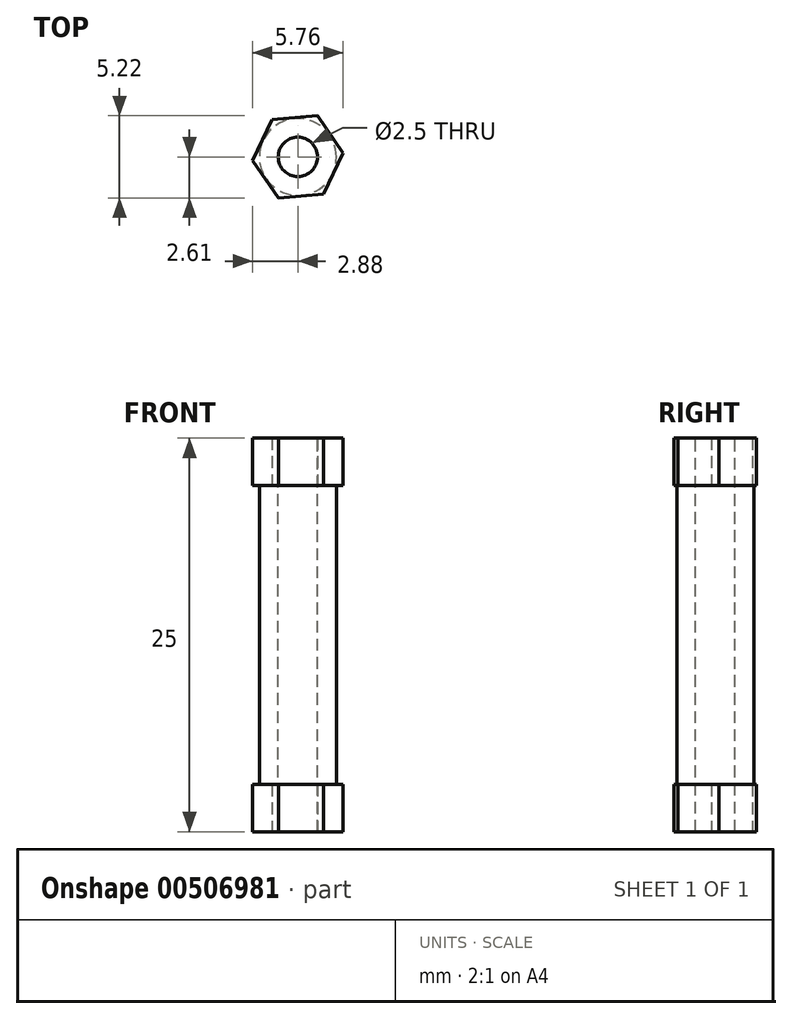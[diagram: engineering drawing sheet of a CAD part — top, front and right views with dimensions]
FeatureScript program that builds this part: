
annotation { "Feature Type Name" : "Feature", "Feature Type Description" : "" }
export const myFeature = defineFeature(function(context is Context, id is Id, definition is map)
    precondition{}
    {
        {
            var Q0;
            Q0=qCreatedBy(makeId("Top.planeOp"),FACE);
            var sketch = newSketch(context, id + "F0", { "sketchPlane" : qUnion([Q0])});
            skCircle(sketch, "E0", {"center": v(0, 0) * mm, "radius": 2.5 * mm, "construction": true});
            skLineSegment(sketch, "E1.0", {"start": v(2.88, 0.24) * mm, "end": v(1.64, -2.37) * mm});
            skLineSegment(sketch, "E1.1", {"start": v(1.64, -2.37) * mm, "end": v(-1.23, -2.6) * mm});
            skLineSegment(sketch, "E1.2", {"start": v(-1.23, -2.6) * mm, "end": v(-2.88, -0.24) * mm});
            skLineSegment(sketch, "E1.3", {"start": v(-2.88, -0.24) * mm, "end": v(-1.64, 2.37) * mm});
            skLineSegment(sketch, "E1.4", {"start": v(-1.64, 2.37) * mm, "end": v(1.23, 2.6) * mm});
            skLineSegment(sketch, "E1.5", {"start": v(1.23, 2.6) * mm, "end": v(2.88, 0.24) * mm});
            skPoint(sketch, "E1.0.midPoint", {"position": v(2.26, -1.07) * mm});
            skSolve(sketch);
        }
        {
            var Q0;
            Q0=makeQuery(id+"F0.imprint","IMPRINT",FACE,{"disambiguationData":[TD([[makeQuery(id+"F0.imprint","IMPRINT",EDGE,{"derivedFrom":sQuery(id+"F0.wireOp",EDGE,"E0")}),1.0]])]});
            var Q1;
            Q1=makeQuery(id+"F0.imprint","IMPRINT",FACE,{"disambiguationData":[TD([[makeQuery(id+"F0.imprint","IMPRINT",EDGE,{"derivedFrom":sQuery(id+"F0.wireOp",EDGE,"E1.0")}),-1.0]])]});
            var Q2;
            Q2=sQuery(id+"F0.wireOp",EDGE,"E0");
            extrude(context, id + "F1", {"entities" : qUnion([Q0, Q1]), "surfaceEntities" : qUnion([Q2]), "depth" : 25 * mm, "offsetDistance" : 25 * mm});
        }
        {
            var Q0;
            Q0=makeQuery(id+"F1.opExtrude","CAP_FACE",FACE,{"disambiguationData":[OSD([sQuery(id+"F0.wireOp",EDGE,"E1.0"),sQuery(id+"F0.wireOp",EDGE,"E1.1"),sQuery(id+"F0.wireOp",EDGE,"E1.2"),sQuery(id+"F0.wireOp",EDGE,"E1.3"),sQuery(id+"F0.wireOp",EDGE,"E1.4"),sQuery(id+"F0.wireOp",EDGE,"E1.5")])],"isStart":false});
            var sketch = newSketch(context, id + "F2", { "sketchPlane" : qUnion([Q0])});
            skPoint(sketch, "E2.0", {"position": v(0, 0) * mm});
            skSolve(sketch);
        }
        {
            var Q0;
            Q0=sQuery(id+"F2.wireOp",VERTEX,"E2.0");
            var Q1;
            Q1=makeQuery(id+"F1.opExtrude","SWEPT_BODY",BODY,{"disambiguationData":[OSD([sQuery(id+"F0.wireOp",EDGE,"E0")])]});
            var Q2;
            Q2=makeQuery(id+"F1.opExtrude","SWEPT_BODY",BODY,{"disambiguationData":[OSD([sQuery(id+"F0.wireOp",EDGE,"E1.0"),sQuery(id+"F0.wireOp",EDGE,"E1.1"),sQuery(id+"F0.wireOp",EDGE,"E1.2"),sQuery(id+"F0.wireOp",EDGE,"E1.3"),sQuery(id+"F0.wireOp",EDGE,"E1.4"),sQuery(id+"F0.wireOp",EDGE,"E1.5")])]});
            hole(context, id + "F3", {"style" : HoleStyle.SIMPLE, "endStyle" : HoleEndStyle.THROUGH, "standardTappedOrClearance" : lookupTablePath({ "standard" : "ISO", "engagement" : "75%", "pitch" : "0.5 mm", "size" : "M3", "type" : "Tapped" }), "standardBlindInLast" : lookupTablePath({ "standard" : "ISO", "engagement" : "75%", "pitch" : "0.5 mm", "size" : "M3", "type" : "Tapped" }), "holeDiameter" : 2.5 * mm, "showTappedDepth" : true, "isTappedThrough" : true, "tappedDepth" : 12 * mm, "tapClearance" : 3, "startFromSketch" : true, "locations" : qUnion([Q0]), "scope" : qUnion([Q1, Q2]), "majorDiameter" : 3 * mm});
        }
        {
            var Q0;
            Q0=qCreatedBy(makeId("Top.planeOp"),FACE);
            cPlane(context, id + "F4", {"entities" : qUnion([Q0]), "cplaneType" : CPlaneType.OFFSET, "offset" : 3 * mm, "width" : 150 * mm, "height" : 150 * mm});
        }
        {
            var Q0;
            Q0=qCreatedBy(id+"F4.planeOp",FACE);
            var sketch = newSketch(context, id + "F5", { "sketchPlane" : qUnion([Q0])});
            skPoint(sketch, "E3.0", {"position": v(0, 0) * mm});
            skCircle(sketch, "E4", {"center": v(0, 0) * mm, "radius": 2.45 * mm});
            skCircle(sketch, "E5", {"center": v(0, 0) * mm, "radius": 12.8 * mm});
            skSolve(sketch);
        }
        {
            var Q0;
            Q0=makeQuery(id+"F5.imprint","IMPRINT",FACE,{"disambiguationData":[TD([[makeQuery(id+"F5.imprint","IMPRINT",EDGE,{"derivedFrom":sQuery(id+"F5.wireOp",EDGE,"E4")}),-1.0]])]});
            extrude(context, id + "F6", {"entities" : qUnion([Q0]), "depth" : (25 - 6) * mm, "offsetDistance" : 25 * mm});
        }
        {
            var Q0;
            Q0=makeQuery(id+"F6.opExtrude","SWEPT_BODY",BODY,{"disambiguationData":[OSD([sQuery(id+"F5.wireOp",EDGE,"E4"),sQuery(id+"F5.wireOp",EDGE,"E5")])]});
            var Q1;
            Q1=makeQuery(id+"F1.opExtrude","SWEPT_BODY",BODY,{"disambiguationData":[OSD([sQuery(id+"F0.wireOp",EDGE,"E1.0"),sQuery(id+"F0.wireOp",EDGE,"E1.1"),sQuery(id+"F0.wireOp",EDGE,"E1.2"),sQuery(id+"F0.wireOp",EDGE,"E1.3"),sQuery(id+"F0.wireOp",EDGE,"E1.4"),sQuery(id+"F0.wireOp",EDGE,"E1.5")])]});
            booleanBodies(context, id + "F7", {"operationType" : BooleanOperationType.SUBTRACTION, "tools" : qUnion([Q0]), "targets" : qUnion([Q1])});
        }
    });
